# Revit family: Casement_28_C_Side_Hung_Standard
name_source: partatom
category: Windows
revit_build: Autodesk Revit 2014 (Build: 20130308_1515(x64)
units: mm (PartAtom-declared; Revit-internal decimal feet)

## types (12) — shared parameters
Aluminium Thickness = 1 mm  [stored 0.00328084 ft]
Bead SG Gap = 13 mm  [stored 0.0426509 ft]
Casement Dimension = 28 mm  [stored 0.0918635 ft]
Custom Sash Left Width = 554 mm  [stored 1.81759 ft]
Custom Sash Right Width = 554 mm  [stored 1.81759 ft]
Default Sill Height = 800 mm  [stored 2.62467 ft]
Depth Bead = 14 mm  [stored 0.0459318 ft]
Depth Mullion = 29 mm  [stored 0.0951444 ft]
Description = Window 28mm, Type C side hung
Frame Center Offset = 14 mm  [stored 0.0459318 ft]
Limit Fixed Pane Width Max = 1500 mm  [stored 4.92126 ft]
Limit Fixed Pane Width Min = 200 mm  [stored 0.656168 ft]
Limit Sash Height Max = 1200 mm
Limit Sash Height Min = 300 mm  [stored 0.984252 ft]
Limit Sash Width Max = 600 mm  [stored 1.9685 ft]
Limit Sash Width Min = 300 mm  [stored 0.984252 ft]
Limit Window Height Max = 1246 mm  [stored 4.08793 ft]
Limit Window Height Min = 346 mm
Limit Window Width Max = 2700 mm
Limit Window Width Min = 1400 mm
Manufacturer = Crealco
Model = Casement 28
Offset Bead Center Reversed = 14 mm  [stored 0.0459318 ft]
Offset Fixed Panel Left = 600 mm  [stored 1.9685 ft]
Offset Mullion Left Side = 570 mm  [stored 1.87008 ft]
Offset Mullion Right Side = 570 mm  [stored 1.87008 ft]
Offset Sash Side = 23 mm  [stored 0.0754593 ft]
Offset Sash Top = 23 mm  [stored 0.0754593 ft]
Offset Window Exterior = 14 mm  [stored 0.0459318 ft]
SG Gasket Thickness = 6 mm  [stored 0.019685 ft]
Sash Center Offset = 11 mm  [stored 0.0360892 ft]
Sash Overlap = 7 mm  [stored 0.0229659 ft]
Sash Spacing Inner = 8 mm  [stored 0.0262467 ft]
Side Hung Left = Yes
Side Hung Right = No
URL = http://www.crealco.co.za
Wall Closure = By host
Width Bead = 15 mm  [stored 0.0492126 ft]
Width Profile = 30 mm  [stored 0.0984252 ft]
Width Sash Left = 554 mm  [stored 1.81759 ft]
Width Sash Left Opening = 524 mm  [stored 1.71916 ft]
Width Sash Right = 554 mm  [stored 1.81759 ft]
Width Sash Right Opening = 524 mm  [stored 1.71916 ft]
zero-valued in all types: Corrected Mullion Size, Standard Mullion Different, Window Exterior Offset

## per-type parameters (varying)
- 28-1809SS-1000Pa: Area Pane Left=0.35 m²; Area Pane Middle=0.48 m²; Area Pane Right=0.35 m²; Clearvue SHGC Value=0.615; Clearvue U Value=6.12; Custom Windload=1000 mm  [stored 3.28084 ft]; Custom Window Height=890 mm  [stored 2.91995 ft]; Custom Window Width=1790 mm  [stored 5.8727 ft]; Energy Advantage SHGC Value=0.556; Energy Advantage U Value=4.63; Height=890 mm  [stored 2.91995 ft]; Height Fixed Panel Center=830 mm  [stored 2.7231 ft]; Height Sash=814 mm  [stored 2.6706 ft]; Height Sash Opening=844 mm  [stored 2.76903 ft]; Intruderprufe LowE SHGC Value=0.543; Intruderprufe LowE U Value=4.4; Intruderprufe SHGC Value=0.596; Intruderprufe U Value=6.1; Length Mullion=890 mm  [stored 2.91995 ft]; Max Pane Area=0.48 m²; Mullion Depth Windload Based=29 mm  [stored 0.0951444 ft]; Sash Height=845 mm  [stored 2.77231 ft]; Width=1790 mm  [stored 5.8727 ft]; Width Fixed Panel Center=590 mm  [stored 1.9357 ft]; Windload Design=1000 mm  [stored 3.28084 ft]
- 28-2409SS-1000Pa: Area Pane Left=0.35 m²; Area Pane Middle=0.97 m²; Area Pane Right=0.35 m²; Clearvue SHGC Value=0.653; Clearvue U Value=6.07; Custom Windload=1000 mm  [stored 3.28084 ft]; Custom Window Height=890 mm  [stored 2.91995 ft]; Custom Window Width=2390 mm; Energy Advantage SHGC Value=0.583; Energy Advantage U Value=4.5; Height=890 mm  [stored 2.91995 ft]; Height Fixed Panel Center=830 mm  [stored 2.7231 ft]; Height Sash=814 mm  [stored 2.6706 ft]; Height Sash Opening=844 mm  [stored 2.76903 ft]; Intruderprufe LowE SHGC Value=0.567; Intruderprufe LowE U Value=4.28; Intruderprufe SHGC Value=0.628; Intruderprufe U Value=6.03; Length Mullion=890 mm  [stored 2.91995 ft]; Max Pane Area=0.97 m²; Mullion Depth Windload Based=29 mm  [stored 0.0951444 ft]; Sash Height=845 mm  [stored 2.77231 ft]; Width=2390 mm; Width Fixed Panel Center=1190 mm  [stored 3.9042 ft]; Windload Design=1000 mm  [stored 3.28084 ft]
- 28-2409SS-2000Pa: Area Pane Left=0.35 m²; Area Pane Middle=0.97 m²; Area Pane Right=0.35 m²; Clearvue SHGC Value=0.653; Clearvue U Value=6.16; Custom Windload=2000 mm  [stored 6.56168 ft]; Custom Window Height=890 mm  [stored 2.91995 ft]; Custom Window Width=2390 mm; Energy Advantage SHGC Value=0.583; Energy Advantage U Value=4.6; Height=890 mm  [stored 2.91995 ft]; Height Fixed Panel Center=830 mm  [stored 2.7231 ft]; Height Sash=814 mm  [stored 2.6706 ft]; Height Sash Opening=844 mm  [stored 2.76903 ft]; Intruderprufe LowE SHGC Value=0.567; Intruderprufe LowE U Value=4.39; Intruderprufe SHGC Value=0.615; Intruderprufe U Value=6.05; Length Mullion=890 mm  [stored 2.91995 ft]; Max Pane Area=0.97 m²; Mullion Depth Windload Based=54 mm  [stored 0.177165 ft]; Sash Height=845 mm  [stored 2.77231 ft]; Width=2390 mm; Width Fixed Panel Center=1190 mm  [stored 3.9042 ft]; Windload Design=2000 mm  [stored 6.56168 ft]
- 28-1812SS-1000Pa: Area Pane Left=0.49 m²; Area Pane Middle=0.65 m²; Area Pane Right=0.49 m²; Clearvue SHGC Value=0.639; Clearvue U Value=6.22; Custom Windload=1000 mm  [stored 3.28084 ft]; Custom Window Height=1190 mm  [stored 3.9042 ft]; Custom Window Width=1790 mm  [stored 5.8727 ft]; Energy Advantage SHGC Value=0.576; Energy Advantage U Value=4.68; Height=1190 mm  [stored 3.9042 ft]; Height Fixed Panel Center=1130 mm  [stored 3.70735 ft]; Height Sash=1114 mm  [stored 3.65486 ft]; Height Sash Opening=1144 mm; Intruderprufe LowE SHGC Value=0.55; Intruderprufe LowE U Value=4.49; Intruderprufe SHGC Value=0.601; Intruderprufe U Value=6.11; Length Mullion=1190 mm  [stored 3.9042 ft]; Max Pane Area=0.65 m²; Mullion Depth Windload Based=54 mm  [stored 0.177165 ft]; Sash Height=1145 mm  [stored 3.75656 ft]; Width=1790 mm  [stored 5.8727 ft]; Width Fixed Panel Center=590 mm  [stored 1.9357 ft]; Windload Design=1000 mm  [stored 3.28084 ft]
- 28-2412SS-1000Pa: Area Pane Left=0.49 m²; Area Pane Middle=1.32 m²; Area Pane Right=0.49 m²; Clearvue SHGC Value=0.676; Clearvue U Value=6.14; Custom Windload=1000 mm  [stored 3.28084 ft]; Custom Window Height=1190 mm  [stored 3.9042 ft]; Custom Window Width=2390 mm; Energy Advantage SHGC Value=0.604; Energy Advantage U Value=4.52; Height=1190 mm  [stored 3.9042 ft]; Height Fixed Panel Center=1130 mm  [stored 3.70735 ft]; Height Sash=1114 mm  [stored 3.65486 ft]; Height Sash Opening=1144 mm; Intruderprufe LowE SHGC Value=0.58; Intruderprufe LowE U Value=4.33; Intruderprufe SHGC Value=0.636; Intruderprufe U Value=6.03; Length Mullion=1190 mm  [stored 3.9042 ft]; Max Pane Area=1.32 m²; Mullion Depth Windload Based=54 mm  [stored 0.177165 ft]; Sash Height=1145 mm  [stored 3.75656 ft]; Width=2390 mm; Width Fixed Panel Center=1190 mm  [stored 3.9042 ft]; Windload Design=1000 mm  [stored 3.28084 ft]
- 28-1809SS-1500Pa: Area Pane Left=0.35 m²; Area Pane Middle=0.48 m²; Area Pane Right=0.35 m²; Clearvue SHGC Value=0.615; Clearvue U Value=6.12; Custom Windload=1500 mm  [stored 4.92126 ft]; Custom Window Height=890 mm  [stored 2.91995 ft]; Custom Window Width=1790 mm  [stored 5.8727 ft]; Energy Advantage SHGC Value=0.556; Energy Advantage U Value=4.63; Height=890 mm  [stored 2.91995 ft]; Height Fixed Panel Center=830 mm  [stored 2.7231 ft]; Height Sash=814 mm  [stored 2.6706 ft]; Height Sash Opening=844 mm  [stored 2.76903 ft]; Intruderprufe LowE SHGC Value=0.543; Intruderprufe LowE U Value=4.4; Intruderprufe SHGC Value=0.596; Intruderprufe U Value=6.1; Length Mullion=890 mm  [stored 2.91995 ft]; Max Pane Area=0.48 m²; Mullion Depth Windload Based=29 mm  [stored 0.0951444 ft]; Sash Height=845 mm  [stored 2.77231 ft]; Width=1790 mm  [stored 5.8727 ft]; Width Fixed Panel Center=590 mm  [stored 1.9357 ft]; Windload Design=1500 mm  [stored 4.92126 ft]
- 28-1809SS-2000Pa: Area Pane Left=0.35 m²; Area Pane Middle=0.48 m²; Area Pane Right=0.35 m²; Clearvue SHGC Value=0.615; Clearvue U Value=6.12; Custom Windload=2000 mm  [stored 6.56168 ft]; Custom Window Height=890 mm  [stored 2.91995 ft]; Custom Window Width=1790 mm  [stored 5.8727 ft]; Energy Advantage SHGC Value=0.556; Energy Advantage U Value=4.63; Height=890 mm  [stored 2.91995 ft]; Height Fixed Panel Center=830 mm  [stored 2.7231 ft]; Height Sash=814 mm  [stored 2.6706 ft]; Height Sash Opening=844 mm  [stored 2.76903 ft]; Intruderprufe LowE SHGC Value=0.543; Intruderprufe LowE U Value=4.4; Intruderprufe SHGC Value=0.596; Intruderprufe U Value=6.1; Length Mullion=890 mm  [stored 2.91995 ft]; Max Pane Area=0.48 m²; Mullion Depth Windload Based=29 mm  [stored 0.0951444 ft]; Sash Height=845 mm  [stored 2.77231 ft]; Width=1790 mm  [stored 5.8727 ft]; Width Fixed Panel Center=590 mm  [stored 1.9357 ft]; Windload Design=2000 mm  [stored 6.56168 ft]
- 28-1812SS-1500Pa: Area Pane Left=0.49 m²; Area Pane Middle=0.65 m²; Area Pane Right=0.49 m²; Clearvue SHGC Value=0.639; Clearvue U Value=6.22; Custom Windload=1500 mm  [stored 4.92126 ft]; Custom Window Height=1190 mm  [stored 3.9042 ft]; Custom Window Width=1790 mm  [stored 5.8727 ft]; Energy Advantage SHGC Value=0.576; Energy Advantage U Value=4.68; Height=1190 mm  [stored 3.9042 ft]; Height Fixed Panel Center=1130 mm  [stored 3.70735 ft]; Height Sash=1114 mm  [stored 3.65486 ft]; Height Sash Opening=1144 mm; Intruderprufe LowE SHGC Value=0.55; Intruderprufe LowE U Value=4.49; Intruderprufe SHGC Value=0.601; Intruderprufe U Value=6.11; Length Mullion=1190 mm  [stored 3.9042 ft]; Max Pane Area=0.65 m²; Mullion Depth Windload Based=54 mm  [stored 0.177165 ft]; Sash Height=1145 mm  [stored 3.75656 ft]; Width=1790 mm  [stored 5.8727 ft]; Width Fixed Panel Center=590 mm  [stored 1.9357 ft]; Windload Design=1500 mm  [stored 4.92126 ft]
- 28-1812SS-2000Pa: Area Pane Left=0.49 m²; Area Pane Middle=0.65 m²; Area Pane Right=0.49 m²; Clearvue SHGC Value=0.639; Clearvue U Value=6.22; Custom Windload=2000 mm  [stored 6.56168 ft]; Custom Window Height=1190 mm  [stored 3.9042 ft]; Custom Window Width=1790 mm  [stored 5.8727 ft]; Energy Advantage SHGC Value=0.576; Energy Advantage U Value=4.68; Height=1190 mm  [stored 3.9042 ft]; Height Fixed Panel Center=1130 mm  [stored 3.70735 ft]; Height Sash=1114 mm  [stored 3.65486 ft]; Height Sash Opening=1144 mm; Intruderprufe LowE SHGC Value=0.55; Intruderprufe LowE U Value=4.49; Intruderprufe SHGC Value=0.601; Intruderprufe U Value=6.11; Length Mullion=1190 mm  [stored 3.9042 ft]; Max Pane Area=0.65 m²; Mullion Depth Windload Based=54 mm  [stored 0.177165 ft]; Sash Height=1145 mm  [stored 3.75656 ft]; Width=1790 mm  [stored 5.8727 ft]; Width Fixed Panel Center=590 mm  [stored 1.9357 ft]; Windload Design=2000 mm  [stored 6.56168 ft]
- 28-2409SS-1500Pa: Area Pane Left=0.35 m²; Area Pane Middle=0.97 m²; Area Pane Right=0.35 m²; Clearvue SHGC Value=0.653; Clearvue U Value=6.07; Custom Windload=1500 mm  [stored 4.92126 ft]; Custom Window Height=890 mm  [stored 2.91995 ft]; Custom Window Width=2390 mm; Energy Advantage SHGC Value=0.583; Energy Advantage U Value=4.5; Height=890 mm  [stored 2.91995 ft]; Height Fixed Panel Center=830 mm  [stored 2.7231 ft]; Height Sash=814 mm  [stored 2.6706 ft]; Height Sash Opening=844 mm  [stored 2.76903 ft]; Intruderprufe LowE SHGC Value=0.567; Intruderprufe LowE U Value=4.28; Intruderprufe SHGC Value=0.628; Intruderprufe U Value=6.03; Length Mullion=890 mm  [stored 2.91995 ft]; Max Pane Area=0.97 m²; Mullion Depth Windload Based=29 mm  [stored 0.0951444 ft]; Sash Height=845 mm  [stored 2.77231 ft]; Width=2390 mm; Width Fixed Panel Center=1190 mm  [stored 3.9042 ft]; Windload Design=1500 mm  [stored 4.92126 ft]
- 28-2412SS-1500Pa: Area Pane Left=0.49 m²; Area Pane Middle=1.32 m²; Area Pane Right=0.49 m²; Clearvue SHGC Value=0.676; Clearvue U Value=6.14; Custom Windload=1500 mm  [stored 4.92126 ft]; Custom Window Height=1190 mm  [stored 3.9042 ft]; Custom Window Width=2390 mm; Energy Advantage SHGC Value=0.604; Energy Advantage U Value=4.52; Height=1190 mm  [stored 3.9042 ft]; Height Fixed Panel Center=1130 mm  [stored 3.70735 ft]; Height Sash=1114 mm  [stored 3.65486 ft]; Height Sash Opening=1144 mm; Intruderprufe LowE SHGC Value=0.58; Intruderprufe LowE U Value=4.33; Intruderprufe SHGC Value=0.636; Intruderprufe U Value=6.03; Length Mullion=1190 mm  [stored 3.9042 ft]; Max Pane Area=1.32 m²; Mullion Depth Windload Based=54 mm  [stored 0.177165 ft]; Sash Height=1145 mm  [stored 3.75656 ft]; Width=2390 mm; Width Fixed Panel Center=1190 mm  [stored 3.9042 ft]; Windload Design=1500 mm  [stored 4.92126 ft]
- 28-2412SS-2000Pa: Area Pane Left=0.49 m²; Area Pane Middle=1.32 m²; Area Pane Right=0.49 m²; Clearvue SHGC Value=0.676; Clearvue U Value=6.14; Custom Windload=2000 mm  [stored 6.56168 ft]; Custom Window Height=1190 mm  [stored 3.9042 ft]; Custom Window Width=2390 mm; Energy Advantage SHGC Value=0.604; Energy Advantage U Value=4.52; Height=1190 mm  [stored 3.9042 ft]; Height Fixed Panel Center=1130 mm  [stored 3.70735 ft]; Height Sash=1114 mm  [stored 3.65486 ft]; Height Sash Opening=1144 mm; Intruderprufe LowE SHGC Value=0.58; Intruderprufe LowE U Value=4.33; Intruderprufe SHGC Value=0.636; Intruderprufe U Value=6.03; Length Mullion=1190 mm  [stored 3.9042 ft]; Max Pane Area=1.32 m²; Mullion Depth Windload Based=54 mm  [stored 0.177165 ft]; Sash Height=1145 mm  [stored 3.75656 ft]; Width=2390 mm; Width Fixed Panel Center=1190 mm  [stored 3.9042 ft]; Windload Design=2000 mm  [stored 6.56168 ft]

note: [stored X ft] marks values corroborated as IEEE doubles in the binary element streams (Revit-internal decimal feet)

## geometry (parser evidence)
native form markers: Sweep x26
no freeform markers — native parametric forms only
